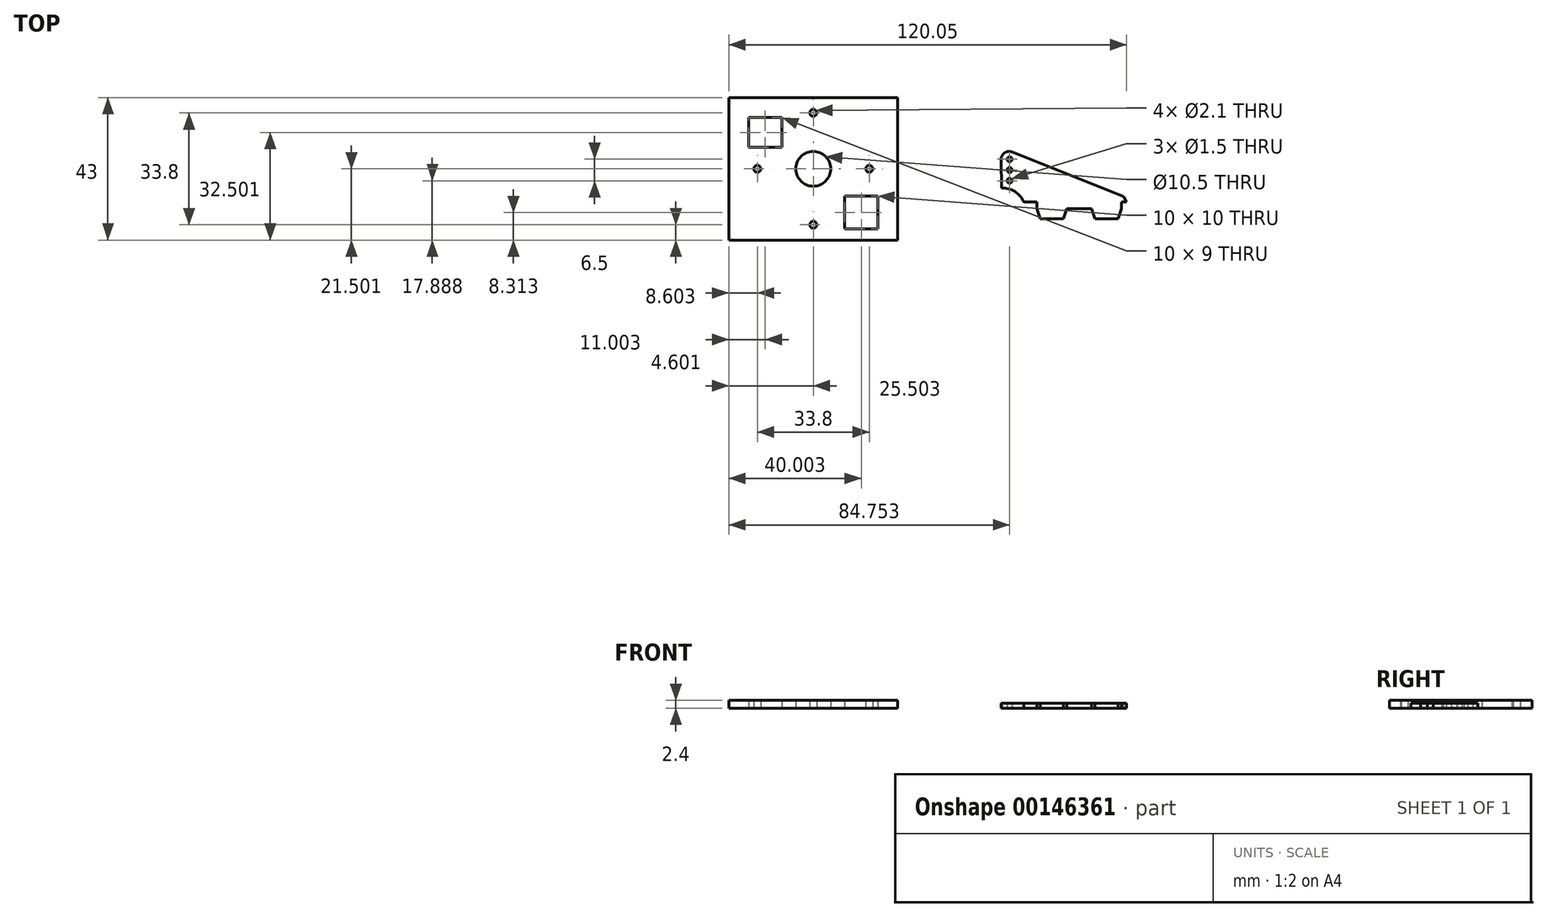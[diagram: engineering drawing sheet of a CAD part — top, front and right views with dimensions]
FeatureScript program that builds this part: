
annotation { "Feature Type Name" : "Feature", "Feature Type Description" : "" }
export const myFeature = defineFeature(function(context is Context, id is Id, definition is map)
    precondition{}
    {
        {
            var Q0;
            Q0=qCreatedBy(makeId("Top.planeOp"),FACE);
            var sketch = newSketch(context, id + "F0", { "sketchPlane" : qUnion([Q0])});
            skLineSegment(sketch, "E0.bottom", {"start": v(-63.57, 61.02) * mm, "end": v(-12.57, 61.02) * mm});
            skLineSegment(sketch, "E0.top", {"start": v(-63.57, 18.02) * mm, "end": v(-12.57, 18.02) * mm});
            skLineSegment(sketch, "E0.left", {"start": v(-63.57, 61.02) * mm, "end": v(-63.57, 18.02) * mm});
            skLineSegment(sketch, "E0.right", {"start": v(-12.57, 61.02) * mm, "end": v(-12.57, 18.02) * mm});
            skLineSegment(sketch, "E1", {"start": v(-38.07, 61.02) * mm, "end": v(-38.07, 18.02) * mm, "construction": true});
            skLineSegment(sketch, "E2", {"start": v(-12.57, 39.52) * mm, "end": v(-63.57, 39.52) * mm, "construction": true});
            skCircle(sketch, "E3", {"center": v(-38.07, 39.52) * mm, "radius": 5.25 * mm});
            skCircle(sketch, "E4", {"center": v(-38.07, 39.52) * mm, "radius": 16.9 * mm, "construction": true});
            skCircle(sketch, "E5", {"center": v(-21.17, 39.52) * mm, "radius": 1.05 * mm});
            skCircle(sketch, "E6", {"center": v(-38.07, 56.42) * mm, "radius": 1.05 * mm});
            skCircle(sketch, "E7", {"center": v(-54.97, 39.52) * mm, "radius": 1.05 * mm});
            skCircle(sketch, "E8", {"center": v(-38.07, 22.62) * mm, "radius": 1.05 * mm});
            skCircle(sketch, "E9", {"center": v(-63.57, 61.02) * mm, "radius": 6 * mm, "construction": true});
            skCircle(sketch, "E10", {"center": v(-12.57, 18.02) * mm, "radius": 6 * mm, "construction": true});
            skLineSegment(sketch, "E11", {"start": v(-63.57, 55.02) * mm, "end": v(-12.57, 55.02) * mm, "construction": true});
            skLineSegment(sketch, "E12", {"start": v(-57.57, 61.02) * mm, "end": v(-57.57, 18.02) * mm, "construction": true});
            skLineSegment(sketch, "E13", {"start": v(-12.57, 24.02) * mm, "end": v(-63.57, 24.02) * mm, "construction": true});
            skLineSegment(sketch, "E14", {"start": v(-18.57, 18.02) * mm, "end": v(-18.57, 61.02) * mm, "construction": true});
            skLineSegment(sketch, "E15.bottom", {"start": v(-57.57, 55.02) * mm, "end": v(-47.57, 55.02) * mm});
            skLineSegment(sketch, "E15.top", {"start": v(-57.57, 46.02) * mm, "end": v(-47.57, 46.02) * mm});
            skLineSegment(sketch, "E15.left", {"start": v(-57.57, 55.02) * mm, "end": v(-57.57, 46.02) * mm});
            skLineSegment(sketch, "E15.right", {"start": v(-47.57, 55.02) * mm, "end": v(-47.57, 46.02) * mm});
            skLineSegment(sketch, "E16.bottom", {"start": v(-18.57, 21.33) * mm, "end": v(-28.57, 21.33) * mm});
            skLineSegment(sketch, "E16.top", {"start": v(-18.57, 31.33) * mm, "end": v(-28.57, 31.33) * mm});
            skLineSegment(sketch, "E16.left", {"start": v(-18.57, 21.33) * mm, "end": v(-18.57, 31.33) * mm});
            skLineSegment(sketch, "E16.right", {"start": v(-28.57, 21.33) * mm, "end": v(-28.57, 31.33) * mm});
            skSolve(sketch);
        }
        {
            var Q0;
            Q0=qCreatedBy(makeId("Top.planeOp"),FACE);
            var sketch = newSketch(context, id + "F1", { "sketchPlane" : qUnion([Q0])});
            skLineSegment(sketch, "E17", {"start": v(25.48, 29.46) * mm, "end": v(56.48, 29.46) * mm, "construction": true});
            skCircle(sketch, "E18", {"center": v(56.48, 29.46) * mm, "radius": 1.5 * mm, "construction": true});
            skCircle(sketch, "E19", {"center": v(25.48, 29.46) * mm, "radius": 4 * mm, "construction": true});
            skCircle(sketch, "E20", {"center": v(25.48, 29.46) * mm, "radius": 17 * mm, "construction": true});
            skCircle(sketch, "E21", {"center": v(56.48, 29.46) * mm, "radius": 41 * mm, "construction": true});
            skLineSegment(sketch, "E22", {"start": v(55.58, 31.22) * mm, "end": v(56.48, 29.46) * mm});
            skLineSegment(sketch, "E23", {"start": v(56.48, 29.46) * mm, "end": v(54.98, 29.46) * mm});
            skLineSegment(sketch, "E24", {"start": v(25.48, 29.46) * mm, "end": v(29.48, 29.46) * mm});
            skCircle(sketch, "E25", {"center": v(25.48, 29.46) * mm, "radius": 8 * mm, "construction": true});
            skCircle(sketch, "E26", {"center": v(56.48, 29.46) * mm, "radius": 38 * mm, "construction": true});
            skLineSegment(sketch, "E27", {"start": v(18.72, 33.74) * mm, "end": v(18.58, 42.22) * mm});
            skPoint(sketch, "E28.visualSharp", {"position": v(18.53, 44.97) * mm});
            skArc(sketch, "E29", {"start": v(25.48, 29.46) * mm, "mid": v(22.77, 32.66) * mm, "end": v(18.72, 33.74) * mm});
            skLineSegment(sketch, "E30", {"start": v(29.48, 29.46) * mm, "end": v(29.48, 27.46) * mm});
            skLineSegment(sketch, "E31", {"start": v(29.48, 27.46) * mm, "end": v(29.48, 24.46) * mm, "construction": true});
            skLineSegment(sketch, "E32", {"start": v(29.48, 24.46) * mm, "end": v(60.66, 24.46) * mm, "construction": true});
            skLineSegment(sketch, "E33", {"start": v(54.98, 29.46) * mm, "end": v(54.98, 27.46) * mm});
            skLineSegment(sketch, "E34", {"start": v(54.98, 27.46) * mm, "end": v(53.98, 27.46) * mm, "construction": true});
            skLineSegment(sketch, "E35", {"start": v(53.98, 27.46) * mm, "end": v(53.98, 23.32) * mm, "construction": true});
            skLineSegment(sketch, "E36", {"start": v(54.98, 27.46) * mm, "end": v(53.98, 24.46) * mm});
            skLineSegment(sketch, "E37", {"start": v(53.98, 24.46) * mm, "end": v(46.98, 24.46) * mm});
            skLineSegment(sketch, "E38", {"start": v(46.98, 24.46) * mm, "end": v(46.98, 27.46) * mm, "construction": true});
            skLineSegment(sketch, "E39", {"start": v(46.98, 27.46) * mm, "end": v(45.98, 27.46) * mm, "construction": true});
            skLineSegment(sketch, "E40", {"start": v(46.98, 24.46) * mm, "end": v(45.98, 27.46) * mm});
            skLineSegment(sketch, "E41", {"start": v(29.48, 27.46) * mm, "end": v(30.48, 27.46) * mm, "construction": true});
            skLineSegment(sketch, "E42", {"start": v(30.48, 27.46) * mm, "end": v(30.48, 24.46) * mm, "construction": true});
            skLineSegment(sketch, "E43", {"start": v(29.48, 27.46) * mm, "end": v(30.48, 24.46) * mm});
            skLineSegment(sketch, "E44", {"start": v(30.48, 24.46) * mm, "end": v(37.48, 24.46) * mm});
            skLineSegment(sketch, "E45", {"start": v(37.48, 24.46) * mm, "end": v(37.48, 27.46) * mm, "construction": true});
            skLineSegment(sketch, "E46", {"start": v(37.48, 27.46) * mm, "end": v(38.48, 27.46) * mm, "construction": true});
            skLineSegment(sketch, "E47", {"start": v(37.48, 24.46) * mm, "end": v(38.48, 27.46) * mm});
            skLineSegment(sketch, "E48", {"start": v(38.48, 27.46) * mm, "end": v(45.98, 27.46) * mm});
            skLineSegment(sketch, "E49", {"start": v(18.68, 35.9) * mm, "end": v(21.18, 35.95) * mm, "construction": true});
            skLineSegment(sketch, "E50", {"start": v(21.18, 33.4) * mm, "end": v(21.18, 46.71) * mm, "construction": true});
            skCircle(sketch, "E51", {"center": v(21.18, 33.4) * mm, "radius": 2.5 * mm, "construction": true});
            skCircle(sketch, "E52", {"center": v(21.18, 35.9) * mm, "radius": 0.75 * mm});
            skCircle(sketch, "E53", {"center": v(21.18, 35.9) * mm, "radius": 3.25 * mm, "construction": true});
            skCircle(sketch, "E54", {"center": v(21.18, 39.16) * mm, "radius": 0.75 * mm});
            skCircle(sketch, "E55", {"center": v(21.18, 39.16) * mm, "radius": 3.25 * mm, "construction": true});
            skCircle(sketch, "E56", {"center": v(21.18, 42.4) * mm, "radius": 0.75 * mm});
            skCircle(sketch, "E57", {"center": v(21.18, 42.4) * mm, "radius": 2.5 * mm, "construction": true});
            skLineSegment(sketch, "E58", {"start": v(55.58, 31.22) * mm, "end": v(22, 44.58) * mm});
            skPoint(sketch, "E59.visualSharp", {"position": v(18.51, 45.97) * mm});
            skArc(sketch, "E59.filletArc", {"start": v(22, 44.58) * mm, "mid": v(19.65, 44.32) * mm, "end": v(18.58, 42.22) * mm});
            skSolve(sketch);
        }
        {
            var Q0;
            Q0=makeQuery(id+"F1.imprint","IMPRINT",FACE,{"disambiguationData":[TD([[makeQuery(id+"F1.imprint","IMPRINT",EDGE,{"derivedFrom":sQuery(id+"F1.wireOp",EDGE,"E22")}),-1.0]])]});
            extrude(context, id + "F2", {"entities" : qUnion([Q0]), "depth" : 1.5 * mm});
        }
        {
            var Q0;
            Q0=makeQuery(id+"F0.imprint","IMPRINT",FACE,{"disambiguationData":[TD([[makeQuery(id+"F0.imprint","IMPRINT",EDGE,{"derivedFrom":sQuery(id+"F0.wireOp",EDGE,"E0.bottom")}),-1.0]])]});
            extrude(context, id + "F3", {"entities" : qUnion([Q0]), "depth" : 2.4 * mm});
        }
    });
